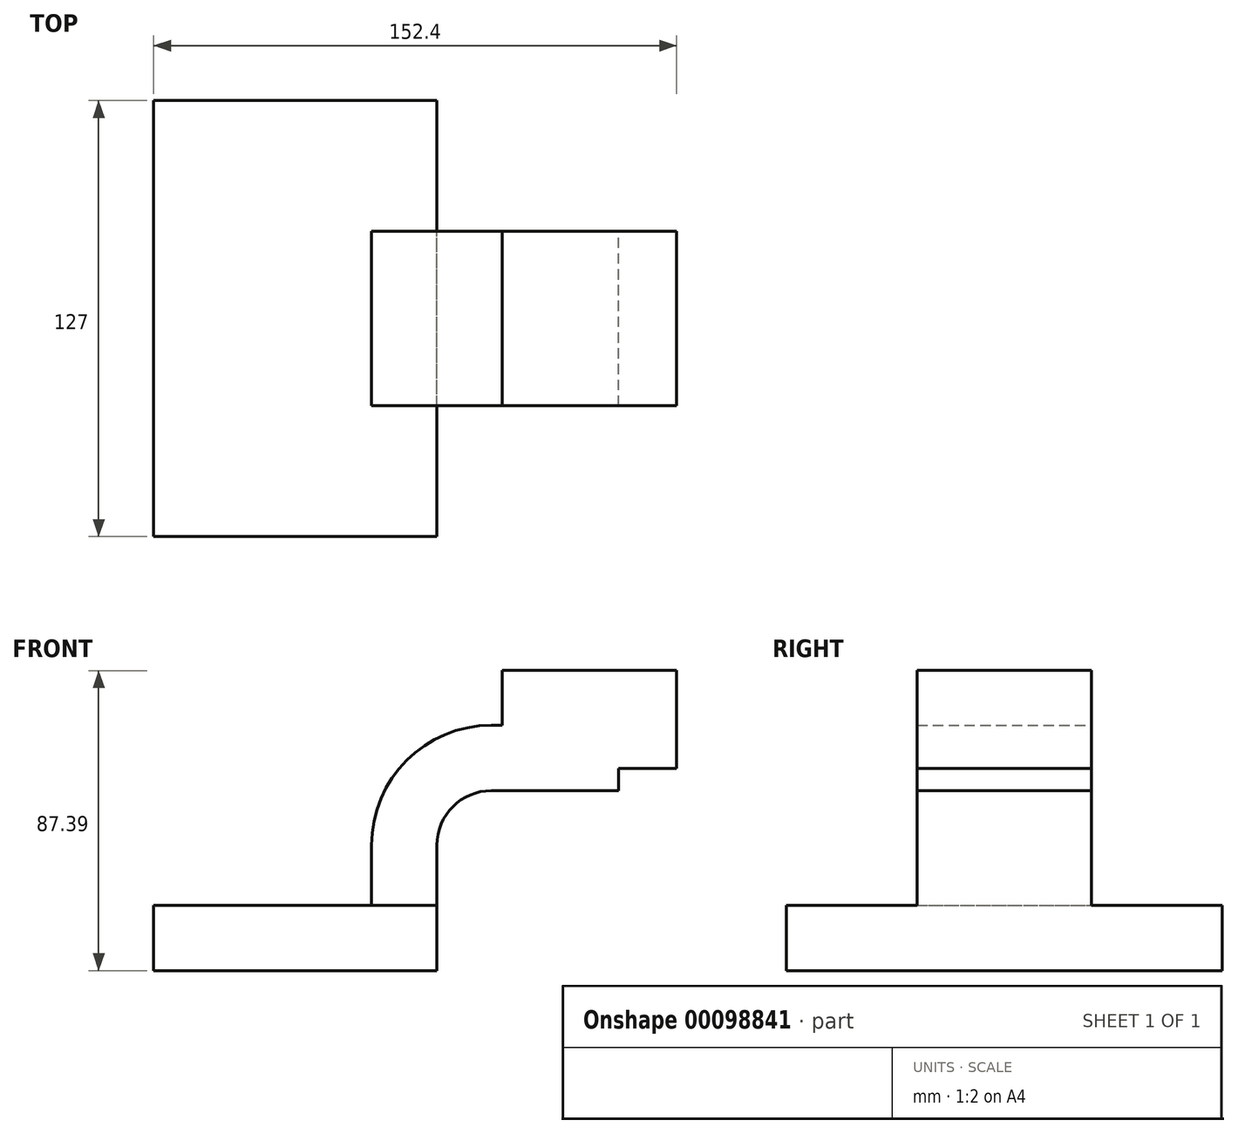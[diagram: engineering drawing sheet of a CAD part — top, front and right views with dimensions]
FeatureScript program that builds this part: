
annotation { "Feature Type Name" : "Feature", "Feature Type Description" : "" }
export const myFeature = defineFeature(function(context is Context, id is Id, definition is map)
    precondition{}
    {
        {
            var Q0;
            Q0=qCreatedBy(makeId("Front.planeOp"),FACE);
            var sketch = newSketch(context, id + "F0", { "sketchPlane" : qUnion([Q0])});
            skLineSegment(sketch, "E0.bottom", {"start": v(-41.28, -9.53) * mm, "end": v(41.28, -9.53) * mm});
            skLineSegment(sketch, "E0.top", {"start": v(-41.28, 9.52) * mm, "end": v(41.28, 9.52) * mm});
            skLineSegment(sketch, "E0.left", {"start": v(-41.28, -9.53) * mm, "end": v(-41.28, 9.52) * mm});
            skLineSegment(sketch, "E0.right", {"start": v(41.28, -9.53) * mm, "end": v(41.28, 9.52) * mm});
            skPoint(sketch, "E0.middle", {"position": v(0, 0) * mm});
            skLineSegment(sketch, "E1.bottom", {"start": v(111.12, 49.29) * mm, "end": v(60.32, 49.29) * mm});
            skLineSegment(sketch, "E1.top", {"start": v(111.12, 77.86) * mm, "end": v(60.32, 77.86) * mm});
            skLineSegment(sketch, "E1.left", {"start": v(111.12, 49.29) * mm, "end": v(111.12, 77.86) * mm});
            skLineSegment(sketch, "E1.right", {"start": v(60.32, 49.29) * mm, "end": v(60.32, 77.86) * mm});
            skPoint(sketch, "E1.middle", {"position": v(85.72, 63.58) * mm});
            skLineSegment(sketch, "E2", {"start": v(41.27, 9.52) * mm, "end": v(41.27, 27) * mm});
            skArc(sketch, "E3", {"start": v(41.27, 27) * mm, "mid": v(45.92, 38.23) * mm, "end": v(57.15, 42.88) * mm});
            skLineSegment(sketch, "E4", {"start": v(57.15, 42.88) * mm, "end": v(94.25, 42.88) * mm});
            skLineSegment(sketch, "E5.0", {"start": v(57.15, 61.93) * mm, "end": v(94.25, 61.93) * mm});
            skArc(sketch, "E5.1", {"start": v(22.22, 27) * mm, "mid": v(32.45, 51.7) * mm, "end": v(57.15, 61.93) * mm});
            skLineSegment(sketch, "E5.2", {"start": v(22.22, 9.52) * mm, "end": v(22.22, 27) * mm});
            skLineSegment(sketch, "E6", {"start": v(94.25, 61.93) * mm, "end": v(94.25, 42.88) * mm});
            skFitSpline(sketch, "E7", {"points": [v(-41.28, 9.53) * mm, v(57.15, 61.93) * mm], "startDerivative": vector(-76.84, 87.62) * mm, "endDerivative": vector(434.25, -66.96) * mm});
            skSolve(sketch);
        }
        {
            var Q0;
            Q0=makeQuery(id+"F0.imprint","IMPRINT",FACE,{"disambiguationData":[TD([[makeQuery(id+"F0.imprint","IMPRINT",EDGE,{"derivedFrom":sQuery(id+"F0.wireOp",EDGE,"E0.bottom")}),1.0]])]});
            extrude(context, id + "F1", {"entities" : qUnion([Q0]), "endBound" : BoundingType.SYMMETRIC, "depth" : 127 * mm});
        }
        {
            var Q0;
            {var subQ0=sQuery(id+"F0.wireOp",EDGE,"E2");Q0=makeQuery(id+"F0.imprint","IMPRINT",FACE,{"disambiguationData":[TD([[makeQuery(id+"F0.imprint","IMPRINT",EDGE,{"derivedFrom":subQ0}),1.0]])]});}
            var Q1;
            {var subQ1=sQuery(id+"F0.wireOp",EDGE,"E1.top");Q1=makeQuery(id+"F0.imprint","IMPRINT",FACE,{"disambiguationData":[TD([[makeQuery(id+"F0.imprint","IMPRINT",EDGE,{"derivedFrom":subQ1}),1.0]])]});}
            var Q2;
            {var subQ0=sQuery(id+"F0.wireOp",EDGE,"E1.right");var subQ1=sQuery(id+"F0.wireOp",EDGE,"E1.bottom");var subQ2=makeQuery(id+"F0.imprint","INTERSECT",VERTEX,{"derivedFrom":[subQ1,subQ0]});Q2=makeQuery(id+"F0.imprint","IMPRINT",FACE,{"disambiguationData":[TD([[makeQuery(id+"F0.imprint","IMPRINT",EDGE,{"disambiguationData":[TD([[subQ2,1.0]])],"derivedFrom":subQ1}),-1.0]])]});}
            extrude(context, id + "F2", {"entities" : qUnion([Q0, Q1, Q2]), "operationType" : NewBodyOperationType.ADD, "endBound" : BoundingType.SYMMETRIC, "depth" : 50.8 * mm});
        }
        {
            var Q0;
            Q0=makeQuery(id+"F0.imprint","IMPRINT",FACE,{"disambiguationData":[TD([[makeQuery(id+"F0.imprint","IMPRINT",EDGE,{"derivedFrom":sQuery(id+"F0.wireOp",EDGE,"E5.1")}),1.0]])]});
            extrude(context, id + "F3", {"entities" : qUnion([Q0]), "operationType" : NewBodyOperationType.ADD, "endBound" : BoundingType.SYMMETRIC, "depth" : 15.88 * mm});
        }
    });
